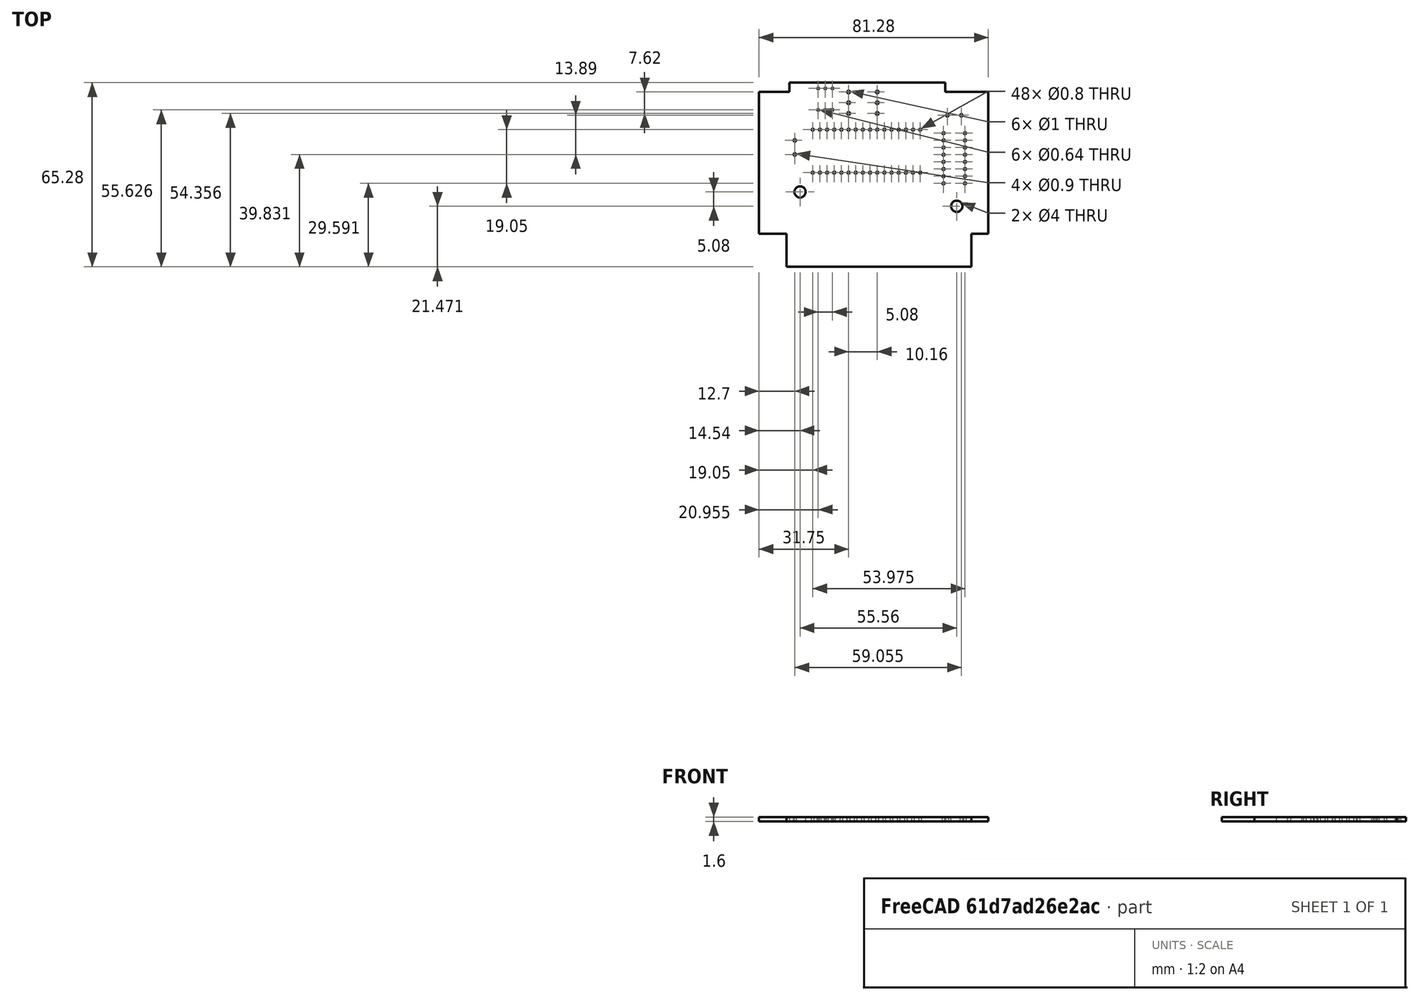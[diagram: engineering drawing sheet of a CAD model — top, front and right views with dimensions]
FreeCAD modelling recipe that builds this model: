
FCSTD DOCUMENT  (FreeCAD 0.20R29177 (Git))
Label: MSX_cart-board
License: All rights reserved
LicenseURL: http://en.wikipedia.org/wiki/All_rights_reserved
objects: Part::Feature×3, Part::Box×2, Part::Cut×2, App::Part×2, PartDesign::CoordinateSystem×1, Sketcher::SketchObject×1
note: 9 computed .brp shape members not serialized (recipe doc carries the construction recipe); baked Part::Feature solids carry a one-line shape summary decoded from their .brp

FEATURE [PartDesign::CoordinateSystem] Local_CS_e656
  AttacherType = Attacher::AttachEngine3D
FEATURE [Part::Feature] Pcb_e656
  Placement = pos=(-111.76,161.036,0) rot=(0,0,1;0rad)
  shape: bbox 81.28 x 65.28 x 1.6 mm, 82 faces (baked)
FEATURE [Sketcher::SketchObject] PCB_Sketch_e656
  FullyConstrained = false
  sketch-geometry (16):
    g0: LineSegment StartX=75.311 StartY=0 StartZ=0 EndX=75.057 EndY=0 EndZ=0
    g1: LineSegment StartX=66.04 StartY=65.278 StartZ=0 EndX=66.04 EndY=61.976 EndZ=0
    g2: LineSegment StartX=10.795 StartY=65.278 StartZ=0 EndX=66.04 EndY=65.278 EndZ=0
    g3: LineSegment StartX=10.795 StartY=65.278 StartZ=0 EndX=10.795 EndY=61.976 EndZ=0
    g4: LineSegment StartX=81.28 StartY=61.976 StartZ=0 EndX=81.28 EndY=11.684 EndZ=0
    g5: LineSegment StartX=75.311 StartY=11.684 StartZ=0 EndX=81.28 EndY=11.684 EndZ=0
    g6: LineSegment StartX=9.779 StartY=0 StartZ=0 EndX=10.033 EndY=0 EndZ=0
    g7: LineSegment StartX=0 StartY=61.976 StartZ=0 EndX=10.795 EndY=61.976 EndZ=0
    g8: LineSegment StartX=75.057 StartY=0 StartZ=0 EndX=10.033 EndY=0 EndZ=0
    g9: LineSegment StartX=0 StartY=11.684 StartZ=0 EndX=0 EndY=61.976 EndZ=0
    g10: LineSegment StartX=75.311 StartY=11.684 StartZ=0 EndX=75.311 EndY=0 EndZ=0
    g11: LineSegment StartX=9.779 StartY=11.684 StartZ=0 EndX=0 EndY=11.684 EndZ=0
    g12: LineSegment StartX=9.779 StartY=0 StartZ=0 EndX=9.779 EndY=11.684 EndZ=0
    g13: LineSegment StartX=66.04 StartY=61.976 StartZ=0 EndX=81.28 EndY=61.976 EndZ=0
    g14: Circle CenterX=70.1 CenterY=21.471 CenterZ=0 NormalX=0 NormalY=0 NormalZ=1 AngleXU=0 Radius=2
    g15: Circle CenterX=14.54 CenterY=26.551 CenterZ=0 NormalX=0 NormalY=0 NormalZ=1 AngleXU=0 Radius=2
  constraints (14):
    c: Coincident(g9,g11)
    c: Coincident(g7,g9)
    c: Coincident(g6,g12)
    c: Coincident(g11,g12)
    c: Coincident(g6,g8)
    c: Coincident(g3,g7)
    c: Coincident(g2,g3)
    c: Coincident(g1,g13)
    c: Coincident(g1,g2)
    c: Coincident(g0,g8)
    c: Coincident(g0,g10)
    c: Coincident(g5,g10)
    c: Coincident(g4,g5)
    c: Coincident(g4,g13)
FEATURE [Part::Feature] pads_area009011001  label="botPads_e656"
  Placement = pos=(-111.76,161.036,-1.62) rot=(0,0,1;0rad)
  shape: bbox 62.51 x 63.41 x 2e-07 mm, 129 faces, 0 solids (baked)
FEATURE [Part::Feature] pads_area009001  label="topPads_e656"
  Placement = pos=(-111.76,161.036,0.02) rot=(0,0,1;0rad)
  shape: bbox 62.51 x 63.41 x 2e-07 mm, 129 faces, 0 solids (baked)
FEATURE [Part::Box] Box  label="Cube"
  AttacherType = Attacher::AttachEngine3D
  Height = 10
  Length = 100
  Placement = pos=(0,13,-5) rot=(0,0,1;0rad)
  Width = 60
FEATURE [Part::Box] Box001  label="Cube001"
  AttacherType = Attacher::AttachEngine3D
  Height = 10
  Length = 100
  Placement = pos=(0,13,-5) rot=(0,0,1;0rad)
  Width = 60
FEATURE [Part::Cut] Cut  label="bot"
  Base = -> pads_area009011001
  Tool = -> Box
FEATURE [Part::Cut] Cut001
  Base = -> pads_area009001
  Tool = -> Box001
FEATURE [App::Part] Board_Geoms_e656
  Group = -> [Local_CS_e656,Pcb_e656,pads_area009001,pads_area009011001,Box,Box001,Cut,Cut001,PCB_Sketch_e656]
  Origin = -> Origin
FEATURE [App::Part] Board_e656  label="rom128k"
  Group = -> [Board_Geoms_e656]
  Origin = -> Origin001
